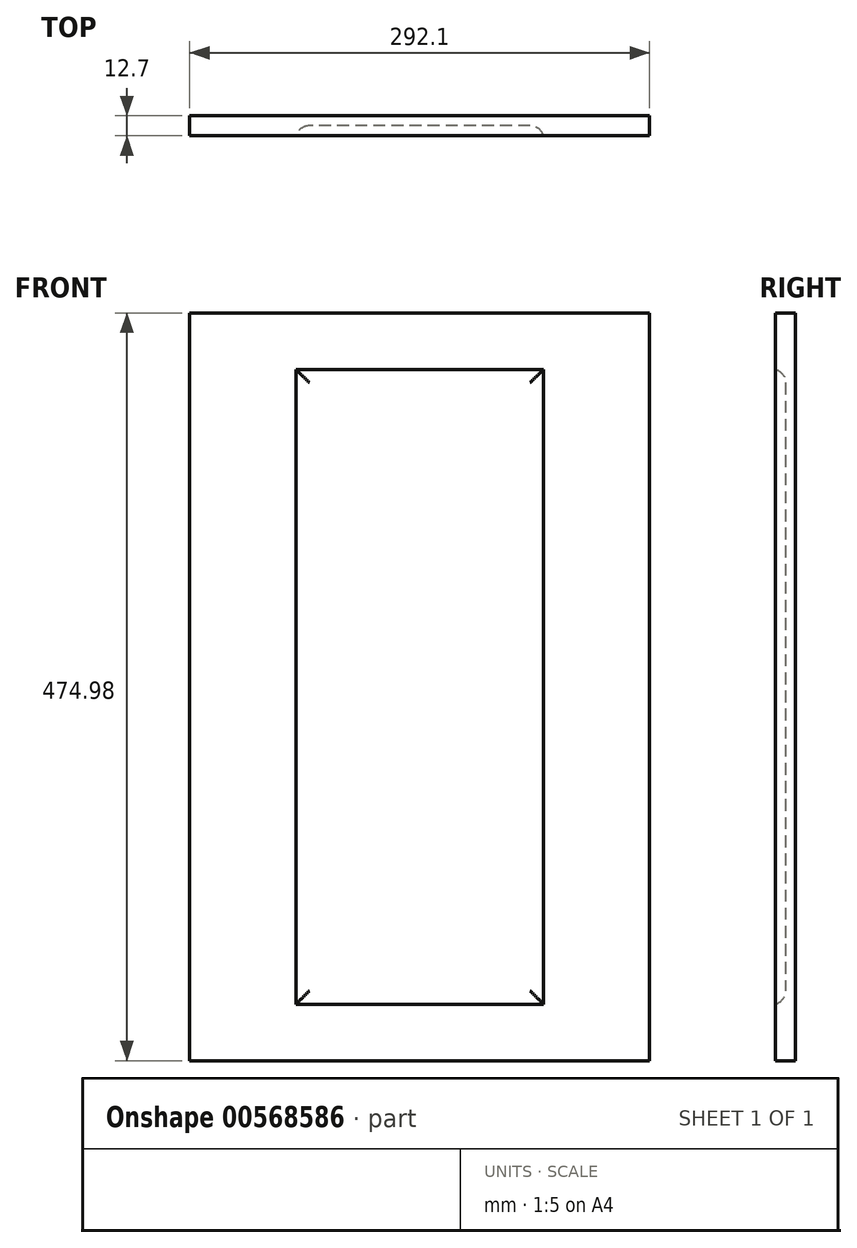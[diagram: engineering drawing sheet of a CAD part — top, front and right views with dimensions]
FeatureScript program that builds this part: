
annotation { "Feature Type Name" : "Feature", "Feature Type Description" : "" }
export const myFeature = defineFeature(function(context is Context, id is Id, definition is map)
    precondition{}
    {
        {
            var Q0;
            Q0=qCreatedBy(makeId("Front.planeOp"),FACE);
            var sketch = newSketch(context, id + "F0", { "sketchPlane" : qUnion([Q0])});
            skLineSegment(sketch, "E0.bottom", {"start": v(146.05, 237.5) * mm, "end": v(-146.05, 237.5) * mm});
            skLineSegment(sketch, "E0.top", {"start": v(146.05, -237.5) * mm, "end": v(-146.05, -237.5) * mm});
            skLineSegment(sketch, "E0.left", {"start": v(146.05, 237.5) * mm, "end": v(146.05, -237.5) * mm});
            skLineSegment(sketch, "E0.right", {"start": v(-146.05, 237.5) * mm, "end": v(-146.05, -237.5) * mm});
            skPoint(sketch, "E0.middle", {"position": v(0, 0) * mm});
            skSolve(sketch);
        }
        {
            var Q0;
            Q0=makeQuery(id+"F0.imprint","IMPRINT",FACE,{"disambiguationData":[TD([[makeQuery(id+"F0.imprint","IMPRINT",EDGE,{"derivedFrom":sQuery(id+"F0.wireOp",EDGE,"E0.bottom")}),1.0]])]});
            extrude(context, id + "F1", {"entities" : qUnion([Q0]), "depth" : 12.7 * mm, "offsetDistance" : 25.4 * mm});
        }
        {
            var Q0;
            Q0=makeQuery(id+"F1.opExtrude","CAP_FACE",FACE,{"disambiguationData":[OSD([sQuery(id+"F0.wireOp",EDGE,"E0.bottom"),sQuery(id+"F0.wireOp",EDGE,"E0.top"),sQuery(id+"F0.wireOp",EDGE,"E0.left"),sQuery(id+"F0.wireOp",EDGE,"E0.right")])],"isStart":false});
            var sketch = newSketch(context, id + "F2", { "sketchPlane" : qUnion([Q0])});
            skLineSegment(sketch, "E1.bottom", {"start": v(78.58, 201.62) * mm, "end": v(-78.58, 201.62) * mm});
            skLineSegment(sketch, "E1.top", {"start": v(78.58, -201.62) * mm, "end": v(-78.58, -201.62) * mm});
            skLineSegment(sketch, "E1.left", {"start": v(78.58, 201.62) * mm, "end": v(78.58, -201.62) * mm});
            skLineSegment(sketch, "E1.right", {"start": v(-78.58, 201.62) * mm, "end": v(-78.58, -201.62) * mm});
            skPoint(sketch, "E1.middle", {"position": v(0, 0) * mm});
            skSolve(sketch);
        }
        {
            var Q0;
            Q0 = qSketchRegion(id + "F2", true);
            extrude(context, id + "F3", {"entities" : qUnion([Q0]), "operationType" : NewBodyOperationType.REMOVE, "oppositeDirection" : true, "depth" : 6.35 * mm, "offsetDistance" : 25.4 * mm});
        }
        {
            var Q0;
            Q0=makeQuery(id+"F3.boolean.opBoolean","COPY",FACE,{"derivedFrom":makeQuery(id+"F3.opExtrude","CAP_FACE",FACE,{"disambiguationData":[OSD([sQuery(id+"F2.wireOp",EDGE,"E1.bottom"),sQuery(id+"F2.wireOp",EDGE,"E1.top"),sQuery(id+"F2.wireOp",EDGE,"E1.left"),sQuery(id+"F2.wireOp",EDGE,"E1.right")])],"isStart":false})});
            fillet(context, id + "F4", {"entities" : qUnion([Q0]), "radius" : 8.9 * mm, "tangentPropagation" : true, "allowEdgeOverflow" : false});
        }
    });
